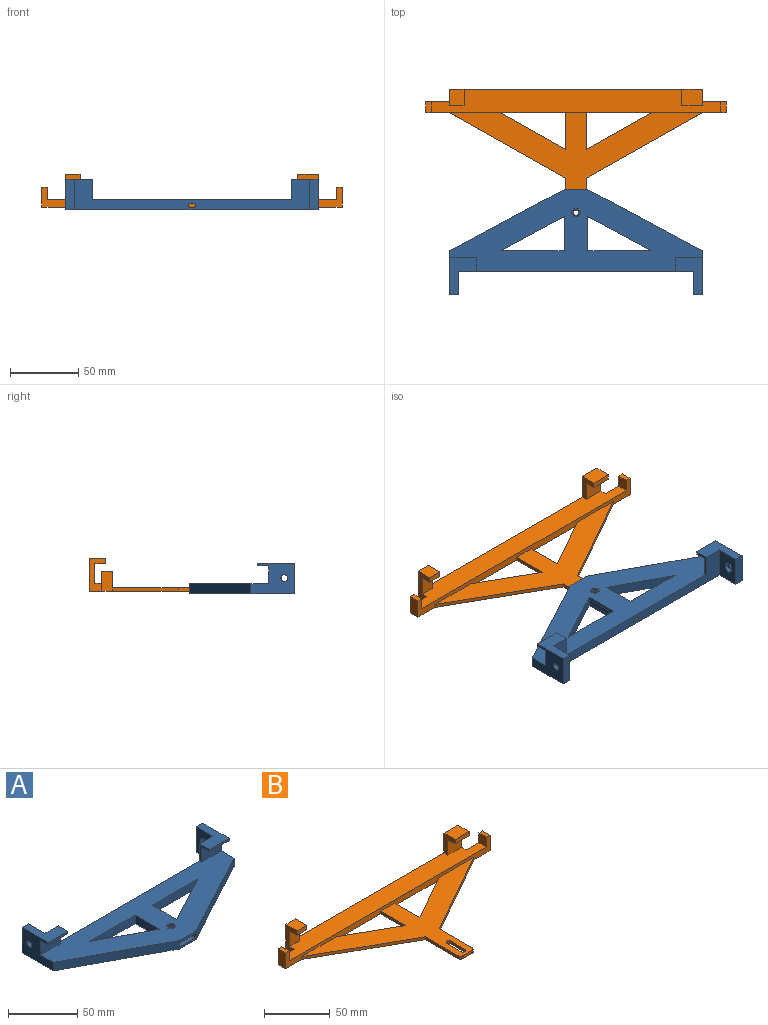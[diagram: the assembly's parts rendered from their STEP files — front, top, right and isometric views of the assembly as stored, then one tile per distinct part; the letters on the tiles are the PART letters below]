
ASSEMBLY  parts=2 mates=1
PART A: 62 faces, bbox 185x77x22.5 mm
  f0: cylinder r=2.5mm len=5mm, axis (1,0,0), area 55mm2, adj f7,f61
  f1: cylinder r=2.5mm len=5mm, axis (-1,0,0), area 55mm2, adj f6,f54
  f2: plane 172x22.5mm, normal (0,1,0), area 1682.1mm2, adj f8,f9,f14,f15,f16,f17,f31,f32
  f3: plane 17.5x7.5mm, normal (0,-1,0), area 73.5mm2, adj f10,f14,f15,f18,f26,f27,f28,f29
  f4: plane 20x2mm, normal (0,-1,0), area 40mm2, adj f7,f8,f9,f24
  f5: plane 20x2mm, normal (0,-1,0), area 40mm2, adj f6,f16,f17,f23
  f6: plane 32x22.5mm, normal (1,0,0), area 521.4mm2, adj f1,f5,f14,f15,f17,f18,f22,f23
  f7: plane 32x22.5mm, normal (-1,0,0), area 521.4mm2, adj f0,f4,f9,f10,f14,f15,f24,f25
  f8: plane 15x10mm, normal (1,0,0), area 46mm2, adj f2,f4,f9,f15,f24,f25
  f9: plane 27x20mm, normal (0,0,1), area 310.5mm2, adj f2,f4,f7,f8,f37,f38
  f10: plane 83.75x45mm, normal (-0.47,-0.88,0), area 713.1mm2, adj f3,f7,f14,f15
  f11: plane 46.53x25mm, normal (0.47,0.88,0), area 396.1mm2, adj f12,f13,f14,f15
  f12: plane 46.53x7.5mm, normal (0,-1,0), area 349mm2, adj f11,f13,f14,f15
  f13: plane 25x7.5mm, normal (-1,0,0), area 187.5mm2, adj f11,f12,f14,f15
  f14: plane 185x77mm, normal (0,0,-1), area 6375.9mm2, adj f2,f3,f6,f7,f10,f11,f12,f13
  f15: plane 185x60mm, normal (0,0,1), area 6056.9mm2, adj f2,f3,f6,f7,f8,f10,f11,f12
  f16: plane 15x10mm, normal (-1,0,0), area 46mm2, adj f2,f5,f15,f17,f22,f23
  f17: plane 27x20mm, normal (0,0,1), area 310.5mm2, adj f2,f5,f6,f16,f35,f36
  f18: plane 83.75x45mm, normal (0.47,-0.88,0), area 713.1mm2, adj f3,f6,f14,f15
  f19: plane 46.53x25mm, normal (-0.47,0.88,0), area 396.1mm2, adj f14,f15,f20,f21
  f20: plane 46.53x7.5mm, normal (0,-1,0), area 349mm2, adj f14,f15,f19,f21
  f21: plane 25x7.5mm, normal (1,0,0), area 187.5mm2, adj f14,f15,f19,f20
  f22: plane 20x13mm, normal (0,-1,0), area 260mm2, adj f6,f15,f16,f23
  f23: plane 20x8mm, normal (0,0,-1), area 160mm2, adj f5,f6,f16,f22
  f24: plane 20x8mm, normal (0,0,-1), area 160mm2, adj f4,f7,f8,f25
  f25: plane 20x13mm, normal (0,-1,0), area 260mm2, adj f7,f8,f15,f24
  f26: plane 40x16.5mm, normal (0,0,-1), area 646.8mm2, adj f3,f27,f29,f30,f46
  f27: plane 40x3.5mm, normal (1,0,0), area 140mm2, adj f3,f26,f28,f30
  f28: plane 40x16.5mm, normal (0,0,1), area 646.8mm2, adj f3,f27,f29,f30,f47
  f29: plane 40x3.5mm, normal (-1,0,0), area 140mm2, adj f3,f26,f28,f30
  f30: plane 16.5x3.5mm, normal (0,-1,0), area 44.8mm2, adj f26,f27,f28,f29,f31,f32,f33,f34
  f31: cylinder r=1.4mm len=20mm, axis (0,-1,0), area 25.9mm2, adj f2,f30,f33,f34
  f32: cylinder r=1.4mm len=20mm, axis (0,-1,0), area 25.9mm2, adj f2,f30,f33,f34
  f33: cylinder r=1.4mm len=20mm, axis (0,-1,0), area 113.9mm2, adj f2,f30,f31,f32
  f34: cylinder r=1.4mm len=20mm, axis (0,-1,0), area 113.9mm2, adj f2,f30,f31,f32
  f35: plane 22.5x17mm, normal (-1,0,0), area 337.6mm2, adj f2,f14,f17,f36,f48,f49,f50,f51
  f36: plane 22.5x6.5mm, normal (0,1,0), area 146.3mm2, adj f6,f14,f17,f35
  f37: plane 22.5x17mm, normal (1,0,0), area 337.6mm2, adj f2,f9,f14,f38,f55,f56,f57,f58
  f38: plane 22.5x6.5mm, normal (0,1,0), area 146.3mm2, adj f7,f9,f14,f37
  f39: plane 3.46x1.7mm, normal (0,-1,0), area 5.9mm2, adj f15,f40,f44,f45
  f40: plane 3x1.73mm, normal (0.87,-0.5,0), area 5.9mm2, adj f15,f39,f41,f45
  f41: plane 3x1.73mm, normal (0.87,0.5,0), area 5.9mm2, adj f15,f40,f42,f45
  f42: plane 3.46x1.7mm, normal (0,1,0), area 5.9mm2, adj f15,f41,f43,f45
  f43: plane 3x1.73mm, normal (-0.87,0.5,0), area 5.9mm2, adj f15,f42,f44,f45
  f44: plane 3x1.73mm, normal (-0.87,-0.5,0), area 5.9mm2, adj f15,f39,f43,f45
  f45: plane 6.93x6mm, normal (0,0,1), area 18mm2, adj f39,f40,f41,f42,f43,f44,f46
  f46: cylinder r=2.05mm len=4.1mm, axis (0,0,1), area 10.3mm2, adj f26,f45
  f47: cylinder r=2.05mm len=4.1mm, axis (0,0,1), area 19.3mm2, adj f14,f28
  f48: plane 3.6x3mm, normal (0,0.5,-0.87), area 12.5mm2, adj f35,f49,f53,f54
  f49: plane 3.6x3mm, normal (0,-0.5,-0.87), area 12.5mm2, adj f35,f48,f50,f54
  f50: plane 4.16x3mm, normal (0,-1,0), area 12.5mm2, adj f35,f49,f51,f54
  f51: plane 3.6x3mm, normal (0,-0.5,0.87), area 12.5mm2, adj f35,f50,f52,f54
  f52: plane 3.6x3mm, normal (0,0.5,0.87), area 12.5mm2, adj f35,f51,f53,f54
  f53: plane 4.16x3mm, normal (0,1,0), area 12.5mm2, adj f35,f48,f52,f54
  f54: plane 8.31x7.2mm, normal (-1,0,0), area 25.3mm2, adj f1,f48,f49,f50,f51,f52,f53
  f55: plane 3.6x3mm, normal (0,-0.5,-0.87), area 12.5mm2, adj f37,f56,f60,f61
  f56: plane 3.6x3mm, normal (0,0.5,-0.87), area 12.5mm2, adj f37,f55,f57,f61
  f57: plane 4.16x3mm, normal (0,1,0), area 12.5mm2, adj f37,f56,f58,f61
  f58: plane 3.6x3mm, normal (0,0.5,0.87), area 12.5mm2, adj f37,f57,f59,f61
  f59: plane 3.6x3mm, normal (0,-0.5,0.87), area 12.5mm2, adj f37,f58,f60,f61
  f60: plane 4.16x3mm, normal (0,-1,0), area 12.5mm2, adj f37,f55,f59,f61
  f61: plane 8.31x7.2mm, normal (1,0,0), area 25.3mm2, adj f0,f55,f56,f57,f58,f59,f60
PART B: 40 faces, bbox 220x103x24.1 mm
  f0: plane 10.5x4mm, normal (0,-1,0), area 42mm2, adj f6,f7,f35,f39
  f1: plane 15x4mm, normal (0,-1,0), area 60mm2, adj f2,f19,f20,f34
  f2: plane 24.1x12mm, normal (1,0,0), area 156.4mm2, adj f1,f3,f5,f14,f20,f25,f33,f34
  f3: plane 220x103mm, normal (0,0,-1), area 7423.3mm2, adj f2,f5,f6,f8,f9,f10,f11,f12
  f4: plane 185x86mm, normal (0,0,1), area 3998.3mm2, adj f8,f9,f10,f11,f12,f13,f21,f22
  f5: plane 185x24.1mm, normal (0,1,0), area 1507.7mm2, adj f2,f3,f6,f7,f14,f19,f20,f39
  f6: plane 24.1x12mm, normal (-1,0,0), area 156.4mm2, adj f0,f3,f5,f7,f14,f15,f35,f36
  f7: plane 12x10.5mm, normal (0,0,1), area 126mm2, adj f0,f5,f6,f39
  f8: plane 85x48mm, normal (-0.49,-0.87,0), area 253.8mm2, adj f3,f4,f9,f12
  f9: plane 35x2.6mm, normal (-1,0,0), area 91mm2, adj f3,f4,f8,f38
  f10: plane 9x2.6mm, normal (0,-1,0), area 23.4mm2, adj f3,f4,f37,f38
  f11: plane 47.81x27mm, normal (0.49,0.87,0), area 142.8mm2, adj f3,f4,f12,f13
  f12: plane 220x14.6mm, normal (0,-1,0), area 1071.6mm2, adj f3,f4,f8,f11,f13,f14,f16,f17
  f13: plane 27x2.6mm, normal (-1,0,0), area 70.2mm2, adj f3,f4,f11,f12
  f14: plane 212x17mm, normal (0,0,1), area 3259mm2, adj f2,f5,f6,f12,f15,f18,f19,f25
  f15: plane 17.5x14.6mm, normal (0,1,0), area 134mm2, adj f3,f6,f14,f16,f17,f18
  f16: plane 8x4mm, normal (0,0,1), area 32mm2, adj f12,f15,f17,f18
  f17: plane 14.6x8mm, normal (-1,0,0), area 116.8mm2, adj f3,f12,f15,f16
  f18: plane 9x8mm, normal (1,0,0), area 72mm2, adj f12,f14,f15,f16
  f19: plane 18.5x12mm, normal (-1,0,0), area 106mm2, adj f1,f5,f14,f20,f33,f34
  f20: plane 15x12mm, normal (0,0,1), area 180mm2, adj f1,f2,f5,f19
  f21: plane 85x48mm, normal (0.49,-0.87,0), area 253.8mm2, adj f3,f4,f12,f22
  f22: plane 35x2.6mm, normal (1,0,0), area 91mm2, adj f3,f4,f21,f37
  f23: plane 47.81x27mm, normal (-0.49,0.87,0), area 142.8mm2, adj f3,f4,f12,f24
  f24: plane 27x2.6mm, normal (1,0,0), area 70.2mm2, adj f3,f4,f12,f23
  f25: plane 17.5x14.6mm, normal (0,1,0), area 134mm2, adj f2,f3,f14,f26,f27,f28
  f26: plane 8x4mm, normal (0,0,1), area 32mm2, adj f12,f25,f27,f28
  f27: plane 14.6x8mm, normal (1,0,0), area 116.8mm2, adj f3,f12,f25,f26
  f28: plane 9x8mm, normal (-1,0,0), area 72mm2, adj f12,f14,f25,f26
  f29: cylinder r=2.1mm len=4.2mm, axis (0,0,1), area 17.2mm2, adj f3,f4,f30,f32
  f30: plane 15x2.6mm, normal (1,0,0), area 39mm2, adj f3,f4,f29,f31
  f31: cylinder r=2.1mm len=4.2mm, axis (0,0,1), area 17.2mm2, adj f3,f4,f30,f32
  f32: plane 15x2.6mm, normal (-1,0,0), area 39mm2, adj f3,f4,f29,f31
  f33: plane 15x14.5mm, normal (0,-1,0), area 217.5mm2, adj f2,f14,f19,f34
  f34: plane 15x8mm, normal (0,0,-1), area 120mm2, adj f1,f2,f19,f33
  f35: plane 10.5x8mm, normal (0,0,-1), area 84mm2, adj f0,f6,f36,f39
  f36: plane 14.5x10.5mm, normal (0,-1,0), area 152.3mm2, adj f6,f14,f35,f39
  f37: cylinder r=3mm len=3mm, axis (0,0,-1), area 12.3mm2, adj f3,f4,f10,f22
  f38: cylinder r=3mm len=3mm, axis (0,0,-1), area 12.3mm2, adj f3,f4,f9,f10
  f39: plane 18.5x12mm, normal (1,0,0), area 106mm2, adj f0,f5,f7,f14,f35,f36
PLACE A rot(axis=(0,0,1),180deg) t=(-17.69,-8.76,4.23)mm
PLACE B t=(-17.69,16.3,5.28)mm
MATE slider A.f31 <-> B.f10  axis (0,1,0) through (-17.69,-41.88,3.98)mm
